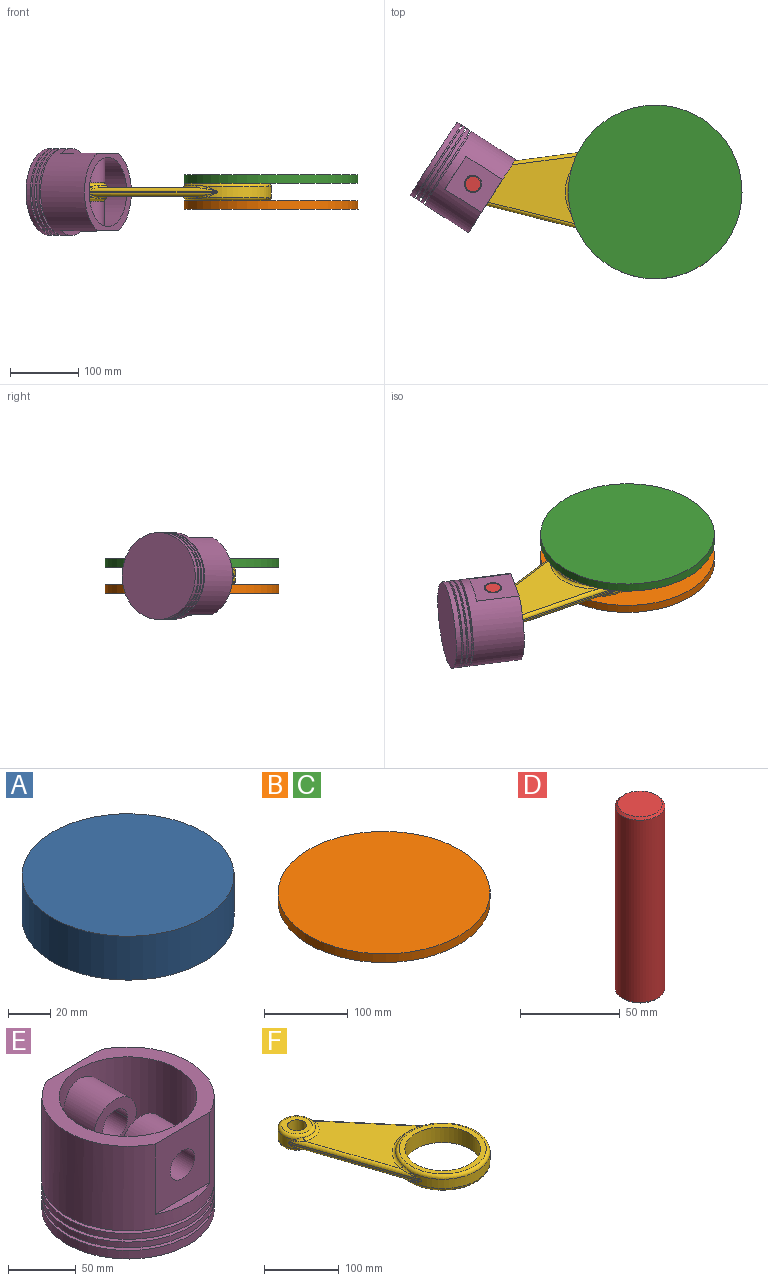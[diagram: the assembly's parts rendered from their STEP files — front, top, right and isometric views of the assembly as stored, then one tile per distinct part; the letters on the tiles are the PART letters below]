
ASSEMBLY  parts=6 mates=6
PART A: 3 faces, bbox 100.3x100.3x25.4 mm
  f0: cylinder r=50.16mm len=100.33mm, axis (0,0,-1), area 8006mm2, adj f1,f2
  f1: plane 100.33x100.33mm, normal (0,0,1), area 7905.9mm2, adj f0
  f2: plane 100.33x100.33mm, normal (0,0,-1), area 7905.9mm2, adj f0
PART B: 3 faces, bbox 254x254x12.7 mm
  f0: cylinder r=127mm len=254mm, axis (0,0,1), area 10134.1mm2, adj f1,f2
  f1: plane 254x254mm, normal (0,0,-1), area 50670.7mm2, adj f0
  f2: plane 254x254mm, normal (0,0,1), area 50670.7mm2, adj f0
PART C: same geometry as B
PART D: 5 faces, bbox 24.9x24.9x114.3 mm
  f0: cylinder r=12.45mm len=111.76mm, axis (0,0,-1), area 8739.7mm2, adj f3,f4
  f1: plane 22.35x22.35mm, normal (0,0,1), area 392.4mm2, adj f4
  f2: plane 22.35x22.35mm, normal (0,0,-1), area 392.4mm2, adj f3
  f3: cone r=12.45mm half-angle=45deg, axis (0,0,1), area 133.3mm2, adj f0,f2
  f4: cone r=11.18mm half-angle=45deg, axis (0,0,-1), area 133.3mm2, adj f0,f1
PART E: 29 faces, bbox 127x127x101.6 mm
  f0: cylinder r=50.8mm len=25.4mm, axis (0,0,1), area 34.5mm2, adj f18,f27
  f1: plane 127x113.41mm, normal (0,0,1), area 4037mm2, adj f10,f12,f14,f16
  f2: cylinder r=63.5mm len=127mm, axis (0,0,-1), area 2026.8mm2, adj f3,f4
  f3: plane 127x127mm, normal (0,0,1), area 2406.9mm2, adj f2,f5
  f4: plane 127x127mm, normal (0,0,-1), area 2359mm2, adj f2,f23
  f5: cylinder r=57.15mm len=114.3mm, axis (0,0,-1), area 912.1mm2, adj f3,f8
  f6: cylinder r=63.5mm len=127mm, axis (0,0,-1), area 2026.8mm2, adj f7,f8
  f7: plane 127x127mm, normal (0,0,1), area 2406.9mm2, adj f6,f9
  f8: plane 127x127mm, normal (0,0,-1), area 2406.9mm2, adj f5,f6
  f9: cylinder r=57.15mm len=114.3mm, axis (0,0,-1), area 912.1mm2, adj f7,f11
  f10: cylinder r=63.5mm len=127mm, axis (0,0,-1), area 22874mm2, adj f1,f11,f14,f15,f16,f17
  f11: plane 127x127mm, normal (0,0,-1), area 2406.9mm2, adj f9,f10
  f12: cylinder r=50.8mm len=101.6mm, axis (0,0,1), area 17086.4mm2, adj f1,f13,f24,f26
  f13: plane 101.6x101.6mm, normal (0,0,1), area 8107.3mm2, adj f12
  f14: plane 63.5x57.15mm, normal (0,-1,0), area 3122.3mm2, adj f1,f10,f15,f19
  f15: plane 57.15x6.79mm, normal (0,0,1), area 261.7mm2, adj f10,f14
  f16: plane 63.5x57.15mm, normal (0,1,0), area 3122.3mm2, adj f1,f10,f17,f18
  f17: plane 57.15x6.79mm, normal (0,0,1), area 261.7mm2, adj f10,f16
  f18: cylinder r=12.7mm len=43.18mm, axis (0,-1,0), area 2038.5mm2, adj f0,f16,f27,f28
  f19: cylinder r=12.7mm len=43.18mm, axis (0,-1,0), area 3445.6mm2, adj f14,f25
  f20: cylinder r=63.5mm len=127mm, axis (0,0,-1), area 3040.2mm2, adj f21,f22
  f21: plane 127x127mm, normal (0,0,1), area 2406.9mm2, adj f20,f23
  f22: plane 127x127mm, normal (0,0,-1), area 12667.7mm2, adj f20
  f23: cone r=57.15mm half-angle=3deg, axis (0,0,1), area 914.4mm2, adj f4,f21
  f24: cylinder r=22.23mm len=44.45mm, axis (0,-1,0), area 4852.5mm2, adj f12,f25
  f25: plane 44.45x44.45mm, normal (0,1,0), area 1045.1mm2, adj f19,f24
  f26: cylinder r=22.23mm len=44.45mm, axis (0,1,0), area 4852.5mm2, adj f12,f28
  f27: cylinder r=12.7mm len=37.27mm, axis (0,1,0), area 1503mm2, adj f0,f18,f28
  f28: plane 44.45x44.45mm, normal (0,-1,0), area 1010.9mm2, adj f18,f26,f27
PART F: 40 faces, bbox 195.9x273.3x25.4 mm
  f0: plane 189.21x63.54mm, normal (-0.95,-0.32,0), area 507mm2, adj f4,f9,f16,f18
  f1: plane 152.51x128.76mm, normal (0.76,0.65,0), area 507mm2, adj f4,f9,f17,f19
  f2: plane 159.51x134.4mm, normal (0,0,1), area 8521.5mm2, adj f18,f19,f27,f37
  f3: plane 159.51x134.4mm, normal (0,0,-1), area 8521.5mm2, adj f16,f17,f22,f32
  f4: cylinder r=25.4mm len=49.54mm, axis (0,0,1), area 1194.2mm2, adj f0,f1,f14,f15,f20,f23,f25,f29
  f5: cylinder r=12.7mm len=25.4mm, axis (0,0,1), area 2026.8mm2, adj f6,f7
  f6: plane 40.64x40.64mm, normal (0,0,-1), area 790.5mm2, adj f5,f15
  f7: plane 40.64x40.64mm, normal (0,0,1), area 790.5mm2, adj f5,f14
  f8: cylinder r=50.8mm len=101.6mm, axis (0,0,-1), area 8107.3mm2, adj f10,f11
  f9: cylinder r=63.5mm len=126.85mm, axis (0,0,-1), area 3611.5mm2, adj f0,f1,f12,f13,f30,f33,f35,f39
  f10: plane 116.84x116.84mm, normal (0,0,1), area 2614.6mm2, adj f8,f13
  f11: plane 116.84x116.84mm, normal (0,0,-1), area 2614.6mm2, adj f8,f12
  f12: torus R=58.42mm, axis (0,0,1), area 2837.3mm2, adj f9,f11,f31,f32,f34
  f13: torus R=58.42mm, axis (0,0,1), area 2837.3mm2, adj f9,f10,f36,f37,f38
  f14: torus R=20.32mm, axis (0,0,1), area 1061.6mm2, adj f4,f7,f26,f27,f28
  f15: torus R=20.32mm, axis (0,0,1), area 1061.6mm2, adj f4,f6,f21,f22,f24
  f16: cylinder r=5.08mm len=190.83mm, axis (0.32,-0.95,0), area 1348.2mm2, adj f0,f3,f23,f24,f30,f31
  f17: cylinder r=5.08mm len=155.78mm, axis (-0.65,0.76,0), area 1348.2mm2, adj f1,f3,f20,f21,f33,f34
  f18: cylinder r=5.08mm len=190.83mm, axis (-0.32,0.95,0), area 1348.2mm2, adj f0,f2,f28,f29,f35,f36
  f19: cylinder r=5.08mm len=155.78mm, axis (0.65,-0.76,0), area 1348.2mm2, adj f1,f2,f25,f26,f38,f39
  f20: bspline ~9.46x6.53mm, area 22.2mm2, adj f4,f17,f21
  f21: bspline ~14.42x6.32mm, area 50.9mm2, adj f15,f17,f20,f22
  f22: torus R=29.74mm, axis (0,0,1), area 306.9mm2, adj f3,f15,f21,f24
  f23: bspline ~11.64x7mm, area 22.2mm2, adj f4,f16,f24
  f24: bspline ~12.89x11.36mm, area 50.9mm2, adj f15,f16,f22,f23
  f25: bspline ~10.64x7.16mm, area 22.2mm2, adj f4,f19,f26
  f26: bspline ~13.12x5.81mm, area 50.9mm2, adj f14,f19,f25,f27
  f27: torus R=29.74mm, axis (0,0,1), area 306.9mm2, adj f2,f14,f26,f28
  f28: bspline ~11.77x10.58mm, area 50.9mm2, adj f14,f18,f27,f29
  f29: bspline ~11.64x7mm, area 22.2mm2, adj f4,f18,f28
  f30: bspline ~16.79x6.35mm, area 31.3mm2, adj f9,f16,f31
  f31: bspline ~23.86x5.79mm, area 79mm2, adj f12,f16,f30,f32
  f32: torus R=67.84mm, axis (0,0,1), area 666.8mm2, adj f3,f12,f31,f34
  f33: bspline ~12.53x12.19mm, area 31.3mm2, adj f9,f17,f34
  f34: bspline ~22.27x16.51mm, area 79mm2, adj f12,f17,f32,f33
  f35: bspline ~16.79x6.35mm, area 31.3mm2, adj f9,f18,f36
  f36: bspline ~25.89x5.79mm, area 79mm2, adj f13,f18,f35,f37
  f37: torus R=67.84mm, axis (0,0,1), area 666.8mm2, adj f2,f13,f36,f38
  f38: bspline ~20.27x15.41mm, area 79mm2, adj f13,f19,f37,f39
  f39: bspline ~12.53x12.19mm, area 31.3mm2, adj f9,f19,f38
PLACE A rot(axis=(-0.13,-0.06,0.99),0deg) t=(-173.92,96.69,168.98)mm
PLACE B rot(axis=(-0.13,-0.06,0.99),0deg) t=(-148.43,147.55,168.98)mm
PLACE C rot(axis=(-0.13,-0.06,0.99),0deg) t=(-148.43,147.55,207.08)mm
PLACE D rot(axis=(0,0,-1),32.7deg) t=(-414.79,159.22,123.69)mm
PLACE E rot(axis=(0.79,0.43,0.43),103.3deg) t=(-472.62,196.29,181.57)mm
PLACE F rot(axis=(0,0,1),57.3deg) t=(-211.93,147.55,181.68)mm
MATE planar C.f0 <-> F.f9  axis (0,0,-1) through (-148.43,147.55,194.38)mm
MATE cylindrical D.f0 <-> E.f18  axis (0,0,-1) through (-414.79,159.22,180.84)mm
MATE cylindrical E.f18 <-> F.f4  axis (0,0,-1) through (-414.79,159.22,146.45)mm
MATE fastened B.f0 <-> A.f2  axis (0,0,1) through (-148.43,147.55,168.98)mm
MATE cylindrical F.f8 <-> A.f0  axis (0,0,-1) through (-211.93,147.55,168.98)mm
MATE fastened A.f0 <-> C.f1  axis (0,0,1) through (-211.93,147.55,194.38)mm
